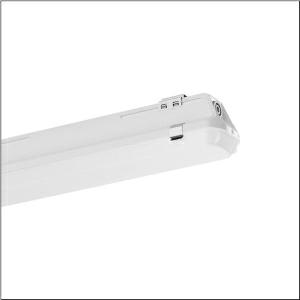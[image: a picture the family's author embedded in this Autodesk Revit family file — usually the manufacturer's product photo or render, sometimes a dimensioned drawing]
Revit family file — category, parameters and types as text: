
# Revit family: monsun_r__21_emergency_51fb207p437b3g_b246
name_source: partatom
category: Lighting Fixtures
units: mm (PartAtom-declared; Revit-internal decimal feet)

## family parameters
Cut with Voids When Loaded = No
Host = Face
Light Source = No
Part Type = Normal
Room Calculation Point = No
Round Connector Dimension = Use Diameter
Shared = No

## types (1)
- Monsun® 21 emergency (1 x LED, 3620 lm, 28 W, 4000K)
    Apparent Load = 28 VA
    CIE Flux Codes = 45 75 93 94 100
    Color Rendering = 80
    Color Temperature = 4000K
    Default Elevation = 1800 mm
    Description = Monsun® 21 emergency, damp-proof luminaire, chain hanger, primary optical cover: enclosure, of PC, light emission: direct distribution, primary light characteristic: symmetric, installation type: vertical mounting, horizontal mounting, surface-mounted, suspended mounting, LED, rated luminous flux: 3.620lm, luminous efficacy: 129lm/W, light colour: 840, colour temperature: 4000K, control gear: ECG, with terminal, 4-pole, max. 2.5mm², mains connection: 220..240V, AC, 50/60Hz, rated input power: 28W, control gear: single battery element, battery: NiCd, 4,5Ah, mains connection: 230V, housing, of glass-fibre reinforced polyester, uncoated, bright grey, incl. chain hanger, length: 1.590mm, width: 90mm, height: 88mm, clip for enclosure, of stainless steel (V2A), ceiling mounting element, of stainless steel (V2A), chain hanger, of stainless steel (V2A), protection rating (complete): IP66, insulation class (complete): insulation class I (protective earthing), certification: CE, UKCA, protection symbol: D, impact resistance: IK08, permissible operating ambient temperature: +5..+25°C, standard: EN 60598-2-1, EN 50419, EN 60598-2-22, corresponds to IFS (International Featured Standards) requirements for safety and quality in the food industry, for indoor or canopied outdoor use, no direct snow, no direct sun, no direct rain, contact your sales advisor before using the luminaires in applications with unclear chemical exposure, large temperature fluctuations or condensation-forming humidity, LABS conformity tested according to VDMA 24364:2018-05, packaging unit: 1 piece
    Height = 89 mm
    Lamp = 1 x LED
    Lamp Light Flux = 3620 lm
    Lamp Power = 28 W
    Lamp count = 1
    Length = 1590 mm
    Luminous efficacy = 129 lm/W
    Manufacturer = Siteco
    ModVariant = No
    Model = 51FB207P437B3G
    Mounting Place = Ceiling
    Mounting Type = Surface mounted
    Number of Poles = 1
    OnlyDefault = Yes
    Power Factor = 1
    Product Name = Monsun® 21 emergency
    Product group = damp-proof luminaire
    ProductGroupID = 300
    Protection Class = Protection class I
    Protection Degree = IP 66
    RLX_Detail_Level = 1
    RLX_Emergency_Light_Flux = 0 lm
    RLX_Emergency_Type = 0
    RLX_Emergency_Type_DB = No
    RlxData = <blob elided: 88749 chars, md5=5968a352>
    Socket = socket
    Standby Power = 0 W
    System Light Flux = 3620 lm
    System Power = 28 W
    Type Comments = Product without accessories
    Type Image = l_1006717.jpg
    URL = http://relux.com
    VarID = ---
    Voltage = 0 V
    Weight = 0.00 kg
    Width = 90 mm

## geometry (parser evidence)
native form markers: Blend x4, Sweep x13
no freeform markers — native parametric forms only
